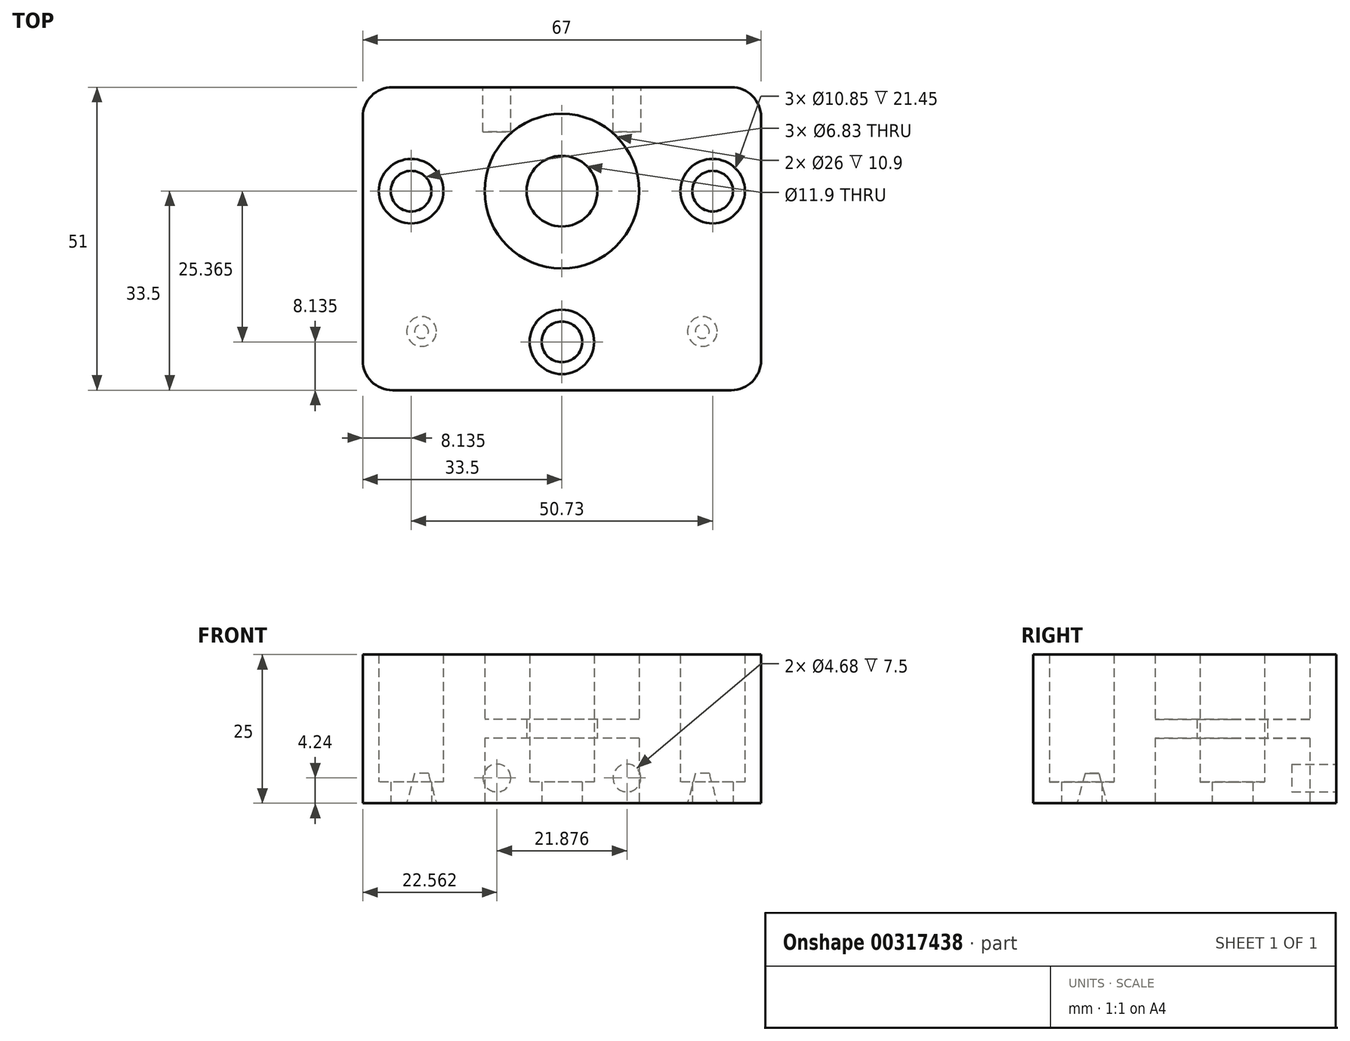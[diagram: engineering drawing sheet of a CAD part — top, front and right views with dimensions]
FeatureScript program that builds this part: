
annotation { "Feature Type Name" : "Feature", "Feature Type Description" : "" }
export const myFeature = defineFeature(function(context is Context, id is Id, definition is map)
    precondition{}
    {
        {
            var Q0;
            Q0=qCreatedBy(makeId("Top.planeOp"),FACE);
            var sketch = newSketch(context, id + "F0", { "sketchPlane" : qUnion([Q0])});
            skLineSegment(sketch, "E0.bottom", {"start": v(-33.5, 17.5) * mm, "end": v(33.5, 17.5) * mm});
            skLineSegment(sketch, "E0.top", {"start": v(-33.5, -33.5) * mm, "end": v(33.5, -33.5) * mm});
            skLineSegment(sketch, "E0.left", {"start": v(-33.5, 17.5) * mm, "end": v(-33.5, -33.5) * mm});
            skLineSegment(sketch, "E0.right", {"start": v(33.5, 17.5) * mm, "end": v(33.5, -33.5) * mm});
            skCircle(sketch, "E1", {"center": v(0, 0) * mm, "radius": 5.95 * mm});
            skCircle(sketch, "E2", {"center": v(25.37, 0) * mm, "radius": 3.42 * mm});
            skCircle(sketch, "E3", {"center": v(-25.37, 0) * mm, "radius": 3.42 * mm});
            skLineSegment(sketch, "E4.bottom", {"start": v(-14.98, 17.5) * mm, "end": v(14.98, 17.5) * mm});
            skLineSegment(sketch, "E4.top", {"start": v(-14.98, -33.5) * mm, "end": v(14.98, -33.5) * mm});
            skLineSegment(sketch, "E4.left", {"start": v(-14.98, 17.5) * mm, "end": v(-14.98, -33.5) * mm});
            skLineSegment(sketch, "E4.right", {"start": v(14.98, 17.5) * mm, "end": v(14.98, -33.5) * mm});
            skCircle(sketch, "E5", {"center": v(-25.37, 0) * mm, "radius": 5.42 * mm});
            skCircle(sketch, "E6", {"center": v(25.37, 0) * mm, "radius": 5.42 * mm});
            skCircle(sketch, "E7", {"center": v(0, -25.37) * mm, "radius": 3.42 * mm});
            skCircle(sketch, "E8", {"center": v(0, -25.37) * mm, "radius": 5.42 * mm});
            skSolve(sketch);
        }
        {
            var Q0;
            Q0=makeQuery(id+"F0.imprint","IMPRINT",FACE,{"disambiguationData":[TD([[makeQuery(id+"F0.imprint","IMPRINT",EDGE,{"derivedFrom":sQuery(id+"F0.wireOp",EDGE,"E1")}),-1.0]])]});
            extrude(context, id + "F1", {"entities" : qUnion([Q0]), "offsetDistance" : 25 * mm, "depth" : 25 * mm});
        }
        {
            var Q0;
            {var subQ1=sQuery(id+"F0.wireOp",EDGE,"E0.left");Q0=makeQuery(id+"F0.imprint","IMPRINT",FACE,{"disambiguationData":[TD([[makeQuery(id+"F0.imprint","IMPRINT",EDGE,{"derivedFrom":subQ1}),1.0]])]});}
            var Q1;
            {var subQ1=sQuery(id+"F0.wireOp",EDGE,"E0.right");Q1=makeQuery(id+"F0.imprint","IMPRINT",FACE,{"disambiguationData":[TD([[makeQuery(id+"F0.imprint","IMPRINT",EDGE,{"derivedFrom":subQ1}),-1.0]])]});}
            extrude(context, id + "F2", {"entities" : qUnion([Q0, Q1]), "operationType" : NewBodyOperationType.ADD, "depth" : 25 * mm});
        }
        {
            var Q0;
            Q0=makeQuery(id+"F0.imprint","IMPRINT",FACE,{"disambiguationData":[TD([[makeQuery(id+"F0.imprint","IMPRINT",EDGE,{"derivedFrom":sQuery(id+"F0.wireOp",EDGE,"E3")}),-1.0]])]});
            var Q1;
            Q1=makeQuery(id+"F0.imprint","IMPRINT",FACE,{"disambiguationData":[TD([[makeQuery(id+"F0.imprint","IMPRINT",EDGE,{"derivedFrom":sQuery(id+"F0.wireOp",EDGE,"E2")}),-1.0]])]});
            var Q2;
            Q2=makeQuery(id+"F0.imprint","IMPRINT",FACE,{"disambiguationData":[TD([[makeQuery(id+"F0.imprint","IMPRINT",EDGE,{"derivedFrom":sQuery(id+"F0.wireOp",EDGE,"E7")}),-1.0]])]});
            extrude(context, id + "F3", {"entities" : qUnion([Q0, Q1, Q2]), "operationType" : NewBodyOperationType.ADD, "depth" : 3.55 * mm});
        }
        {
            var Q0;
            {var subQ0=sQuery(id+"F0.wireOp",EDGE,"E0.bottom");var subQ1=sQuery(id+"F0.wireOp",EDGE,"E4.bottom");var subQ2=makeQuery(id+"F0.imprint","IMPRINT",EDGE,{"disambiguationData":[TD([[makeQuery(id+"F0.imprint","INTERSECT",VERTEX,{"derivedFrom":[subQ0,sQuery(id+"F0.wireOp",EDGE,"E0.right")]}),1.0]])],"derivedFrom":subQ0});var subQ3=makeQuery(id+"F0.imprint","IMPRINT",EDGE,{"disambiguationData":[TD([[makeQuery(id+"F0.imprint","INTERSECT",VERTEX,{"derivedFrom":[subQ0,sQuery(id+"F0.wireOp",EDGE,"E0.left")]}),-1.0]])],"derivedFrom":subQ0});Q0=makeQuery(id+"FTeboLwCj6z0h2F_3.boolean.opBoolean","MERGE",FACE,{"derivedFrom":[makeQuery(id+"FI1iS4n02Gt5v50_0.boolean.opBoolean","MERGE",FACE,{"derivedFrom":[makeQuery(id+"F2.boolean.opBoolean","MERGE",FACE,{"derivedFrom":[makeQuery(id+"F1.opExtrude","SWEPT_FACE",FACE,{"disambiguationData":[OSD([subQ1])]}),makeQuery(id+"F2.opExtrude","SWEPT_FACE",FACE,{"disambiguationData":[OSD([subQ0]),TDD([subQ3])]}),makeQuery(id+"F2.opExtrude","SWEPT_FACE",FACE,{"disambiguationData":[OSD([subQ0]),TDD([subQ2])]})]}),makeQuery(id+"FI1iS4n02Gt5v50_0.opExtrude","SWEPT_FACE",FACE,{"disambiguationData":[OSD([subQ0,subQ1])]})]}),makeQuery(id+"FTeboLwCj6z0h2F_3.opExtrude","SWEPT_FACE",FACE,{"disambiguationData":[OSD([subQ0]),TDD([subQ3])]}),makeQuery(id+"FTeboLwCj6z0h2F_3.opExtrude","SWEPT_FACE",FACE,{"disambiguationData":[OSD([subQ0]),TDD([subQ2])]})]});}
            var sketch = newSketch(context, id + "F4", { "sketchPlane" : qUnion([Q0])});
            skCircle(sketch, "E9", {"center": v(-10.94, 4.24) * mm, "radius": 2.34 * mm});
            skCircle(sketch, "E10", {"center": v(10.94, 4.24) * mm, "radius": 2.34 * mm});
            skSolve(sketch);
        }
        {
            var Q0;
            Q0=makeQuery(id+"F4.imprint","IMPRINT",FACE,{"disambiguationData":[TD([[makeQuery(id+"F4.imprint","IMPRINT",EDGE,{"derivedFrom":sQuery(id+"F4.wireOp",EDGE,"E9")}),1.0]])]});
            var Q1;
            Q1=makeQuery(id+"F4.imprint","IMPRINT",FACE,{"disambiguationData":[TD([[makeQuery(id+"F4.imprint","IMPRINT",EDGE,{"derivedFrom":sQuery(id+"F4.wireOp",EDGE,"E10")}),1.0]])]});
            var Q2;
            Q2=sQuery(id+"F4.wireOp",EDGE,"E9");
            var Q3;
            Q3=sQuery(id+"F4.wireOp",EDGE,"E10");
            extrude(context, id + "F5", {"entities" : qUnion([Q0, Q1]), "operationType" : NewBodyOperationType.REMOVE, "surfaceEntities" : qUnion([Q2, Q3]), "oppositeDirection" : true, "depth" : 7.5 * mm});
        }
        {
            var Q0;
            Q0=qCreatedBy(makeId("Top.planeOp"),FACE);
            var sketch = newSketch(context, id + "F6", { "sketchPlane" : qUnion([Q0])});
            skCircle(sketch, "E11", {"center": v(0, 0) * mm, "radius": 13 * mm});
            skSolve(sketch);
        }
        {
            var Q0;
            Q0=qSketchRegion(id+"F6",true);
            extrude(context, id + "F7", {"entities" : qUnion([Q0]), "operationType" : NewBodyOperationType.REMOVE, "depth" : 25 * mm, "hasSecondDirection" : true, "secondDirectionOppositeDirection" : false, "secondDirectionDepth" : 14.1 * mm});
        }
        {
            var Q0;
            Q0=qSketchRegion(id+"F6",true);
            extrude(context, id + "F8", {"entities" : qUnion([Q0]), "operationType" : NewBodyOperationType.REMOVE, "depth" : 10.9 * mm});
        }
        {
            var Q0;
            Q0=qCreatedBy(makeId("Top.planeOp"),FACE);
            var sketch = newSketch(context, id + "F9", { "sketchPlane" : qUnion([Q0])});
            skLineSegment(sketch, "E12.rect.bottom", {"start": v(-28.11, 28.11) * mm, "end": v(28.12, 28.11) * mm});
            skLineSegment(sketch, "E12.rect.top", {"start": v(-28.12, -28.11) * mm, "end": v(28.11, -28.11) * mm});
            skLineSegment(sketch, "E12.rect.left", {"start": v(-28.11, 28.12) * mm, "end": v(-28.12, -28.11) * mm});
            skLineSegment(sketch, "E12.rect.right", {"start": v(28.12, 28.12) * mm, "end": v(28.11, -28.11) * mm});
            skPoint(sketch, "E12.rect.middle", {"position": v(0, 0) * mm});
            skCircle(sketch, "E13", {"center": v(0, 0) * mm, "radius": 19.04 * mm});
            skCircle(sketch, "E14", {"center": v(0, 0) * mm, "radius": 3.98 * mm});
            skCircle(sketch, "E15", {"center": v(-23.62, 23.62) * mm, "radius": 2.5 * mm});
            skCircle(sketch, "E16", {"center": v(23.62, 23.62) * mm, "radius": 2.5 * mm});
            skCircle(sketch, "E17", {"center": v(23.62, -23.62) * mm, "radius": 2.5 * mm});
            skCircle(sketch, "E18", {"center": v(-23.62, -23.62) * mm, "radius": 2.5 * mm});
            skLineSegment(sketch, "E19.rect.bottom", {"start": v(-23.62, 23.62) * mm, "end": v(23.62, 23.62) * mm, "construction": true});
            skLineSegment(sketch, "E19.rect.top", {"start": v(-23.62, -23.62) * mm, "end": v(23.62, -23.62) * mm, "construction": true});
            skLineSegment(sketch, "E19.rect.left", {"start": v(-23.62, 23.62) * mm, "end": v(-23.62, -23.62) * mm, "construction": true});
            skLineSegment(sketch, "E19.rect.right", {"start": v(23.62, 23.62) * mm, "end": v(23.62, -23.62) * mm, "construction": true});
            skCircle(sketch, "E20", {"center": v(0, 0) * mm, "radius": 5.38 * mm});
            skSolve(sketch);
        }
        {
            var Q0;
            Q0=makeQuery(id+"F9.imprint","IMPRINT",FACE,{"disambiguationData":[TD([[makeQuery(id+"F9.imprint","IMPRINT",EDGE,{"derivedFrom":sQuery(id+"F9.wireOp",EDGE,"E17")}),1.0]])]});
            var Q1;
            Q1=makeQuery(id+"F9.imprint","IMPRINT",FACE,{"disambiguationData":[TD([[makeQuery(id+"F9.imprint","IMPRINT",EDGE,{"derivedFrom":sQuery(id+"F9.wireOp",EDGE,"E18")}),1.0]])]});
            var Q2;
            Q2=sQuery(id+"F9.wireOp",EDGE,"E17");
            var Q3;
            Q3=sQuery(id+"F9.wireOp",EDGE,"E18");
            extrude(context, id + "F10", {"entities" : qUnion([Q0, Q1]), "operationType" : NewBodyOperationType.REMOVE, "surfaceEntities" : qUnion([Q2, Q3]), "depth" : 5 * mm, "hasDraft" : true, "draftAngle" : 15 * degree, "draftPullDirection" : true});
        }
        {
            var Q0;
            Q0=makeQuery(id+"F2.opExtrude","SWEPT_EDGE",EDGE,{"disambiguationData":[OSD([sQuery(id+"F0.wireOp",EDGE,"E0.top"),sQuery(id+"F0.wireOp",EDGE,"E0.right")])]});
            var Q1;
            Q1=makeQuery(id+"F2.opExtrude","SWEPT_EDGE",EDGE,{"disambiguationData":[OSD([sQuery(id+"F0.wireOp",EDGE,"E0.top"),sQuery(id+"F0.wireOp",EDGE,"E0.left")])]});
            var Q2;
            Q2=makeQuery(id+"F2.opExtrude","SWEPT_EDGE",EDGE,{"disambiguationData":[OSD([sQuery(id+"F0.wireOp",EDGE,"E0.bottom"),sQuery(id+"F0.wireOp",EDGE,"E0.left")])]});
            var Q3;
            Q3=makeQuery(id+"F2.opExtrude","SWEPT_EDGE",EDGE,{"disambiguationData":[OSD([sQuery(id+"F0.wireOp",EDGE,"E0.bottom"),sQuery(id+"F0.wireOp",EDGE,"E0.right")])]});
            fillet(context, id + "F11", {"entities" : qUnion([Q0, Q1, Q2, Q3]), "radius" : 5 * mm, "tangentPropagation" : true, "allowEdgeOverflow" : false});
        }
    });
